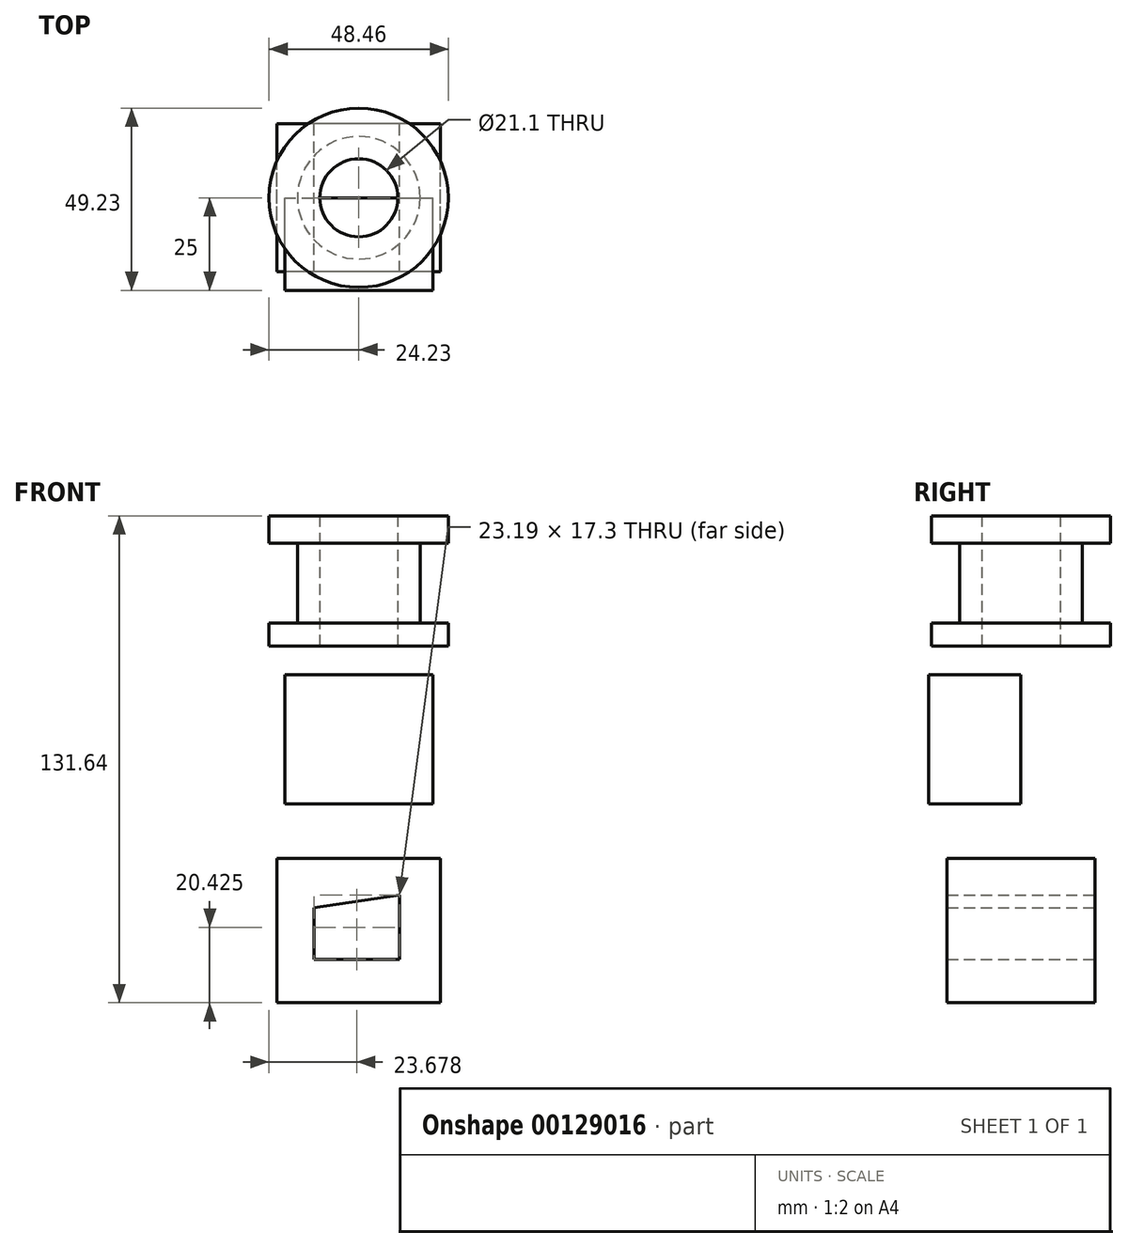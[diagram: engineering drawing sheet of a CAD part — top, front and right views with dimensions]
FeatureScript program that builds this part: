
annotation { "Feature Type Name" : "Feature", "Feature Type Description" : "" }
export const myFeature = defineFeature(function(context is Context, id is Id, definition is map)
    precondition{}
    {
        {
            var Q0;
            Q0=qCreatedBy(makeId("Front.planeOp"),FACE);
            var sketch = newSketch(context, id + "F0", { "sketchPlane" : qUnion([Q0])});
            skLineSegment(sketch, "E0.bottom", {"start": v(-20, -17.5) * mm, "end": v(20, -17.5) * mm});
            skLineSegment(sketch, "E0.top", {"start": v(-20, 17.5) * mm, "end": v(20, 17.5) * mm});
            skLineSegment(sketch, "E0.left", {"start": v(-20, -17.5) * mm, "end": v(-20, 17.5) * mm});
            skLineSegment(sketch, "E0.right", {"start": v(20, -17.5) * mm, "end": v(20, 17.5) * mm});
            skPoint(sketch, "E0.middle", {"position": v(0, 0) * mm});
            skSolve(sketch);
        }
        {
            var Q0;
            Q0 = qSketchRegion(id + "F0", true);
            extrude(context, id + "F1", {"entities" : qUnion([Q0]), "depth" : 25 * mm});
        }
        {
            var Q0;
            Q0=qCreatedBy(makeId("Right.planeOp"),FACE);
            var sketch = newSketch(context, id + "F2", { "sketchPlane" : qUnion([Q0])});
            skLineSegment(sketch, "E1", {"start": v(0, 0) * mm, "end": v(0, 65.05) * mm, "construction": true});
            skLineSegment(sketch, "E2.bottom", {"start": v(-24.23, 60.42) * mm, "end": v(-10.55, 60.42) * mm});
            skLineSegment(sketch, "E2.top", {"start": v(-24.23, 25.17) * mm, "end": v(-10.55, 25.17) * mm});
            skLineSegment(sketch, "E2.left", {"start": v(-24.23, 60.42) * mm, "end": v(-24.23, 53) * mm});
            skLineSegment(sketch, "E2.right", {"start": v(-10.55, 60.42) * mm, "end": v(-10.55, 25.17) * mm});
            skLineSegment(sketch, "E3", {"start": v(-24.23, 53) * mm, "end": v(-16.58, 53) * mm});
            skLineSegment(sketch, "E4", {"start": v(-16.58, 53) * mm, "end": v(-16.58, 31.43) * mm});
            skLineSegment(sketch, "E5", {"start": v(-16.58, 31.43) * mm, "end": v(-24.23, 31.43) * mm});
            skLineSegment(sketch, "E6.trimOffspring", {"start": v(-24.23, 31.43) * mm, "end": v(-24.23, 25.17) * mm});
            skSolve(sketch);
        }
        {
            var Q0;
            Q0 = qSketchRegion(id + "F2", true);
            var Q1;
            Q1=sQuery(id+"F2.wireOp",EDGE,"E1");
            revolve(context, id + "F3", {"entities" : qUnion([Q0]), "axis" : qUnion([Q1]), "revolveType" : RevolveType.FULL});
        }
        {
            var Q0;
            Q0=qCreatedBy(makeId("Front.planeOp"),FACE);
            var sketch = newSketch(context, id + "F4", { "sketchPlane" : qUnion([Q0])});
            skLineSegment(sketch, "E7.bottom", {"start": v(22.08, -32.2) * mm, "end": v(-22.08, -32.2) * mm});
            skLineSegment(sketch, "E7.top", {"start": v(22.08, -71.22) * mm, "end": v(-22.08, -71.22) * mm});
            skLineSegment(sketch, "E7.left", {"start": v(22.08, -32.2) * mm, "end": v(22.08, -71.22) * mm});
            skLineSegment(sketch, "E7.right", {"start": v(-22.08, -32.2) * mm, "end": v(-22.08, -71.22) * mm});
            skPoint(sketch, "E7.middle", {"position": v(0, -51.72) * mm});
            skLineSegment(sketch, "E8", {"start": v(-12.15, -45.46) * mm, "end": v(-12.15, -59.44) * mm});
            skLineSegment(sketch, "E9", {"start": v(-12.15, -59.44) * mm, "end": v(11.04, -59.44) * mm});
            skLineSegment(sketch, "E10", {"start": v(11.04, -59.44) * mm, "end": v(11.04, -42.15) * mm});
            skLineSegment(sketch, "E11", {"start": v(11.04, -42.15) * mm, "end": v(-12.15, -45.46) * mm});
            skSolve(sketch);
        }
        {
            var Q0;
            Q0 = qSketchRegion(id + "F4", true);
            extrude(context, id + "F5", {"entities" : qUnion([Q0]), "endBound" : BoundingType.SYMMETRIC, "depth" : 40 * mm});
        }
    });
